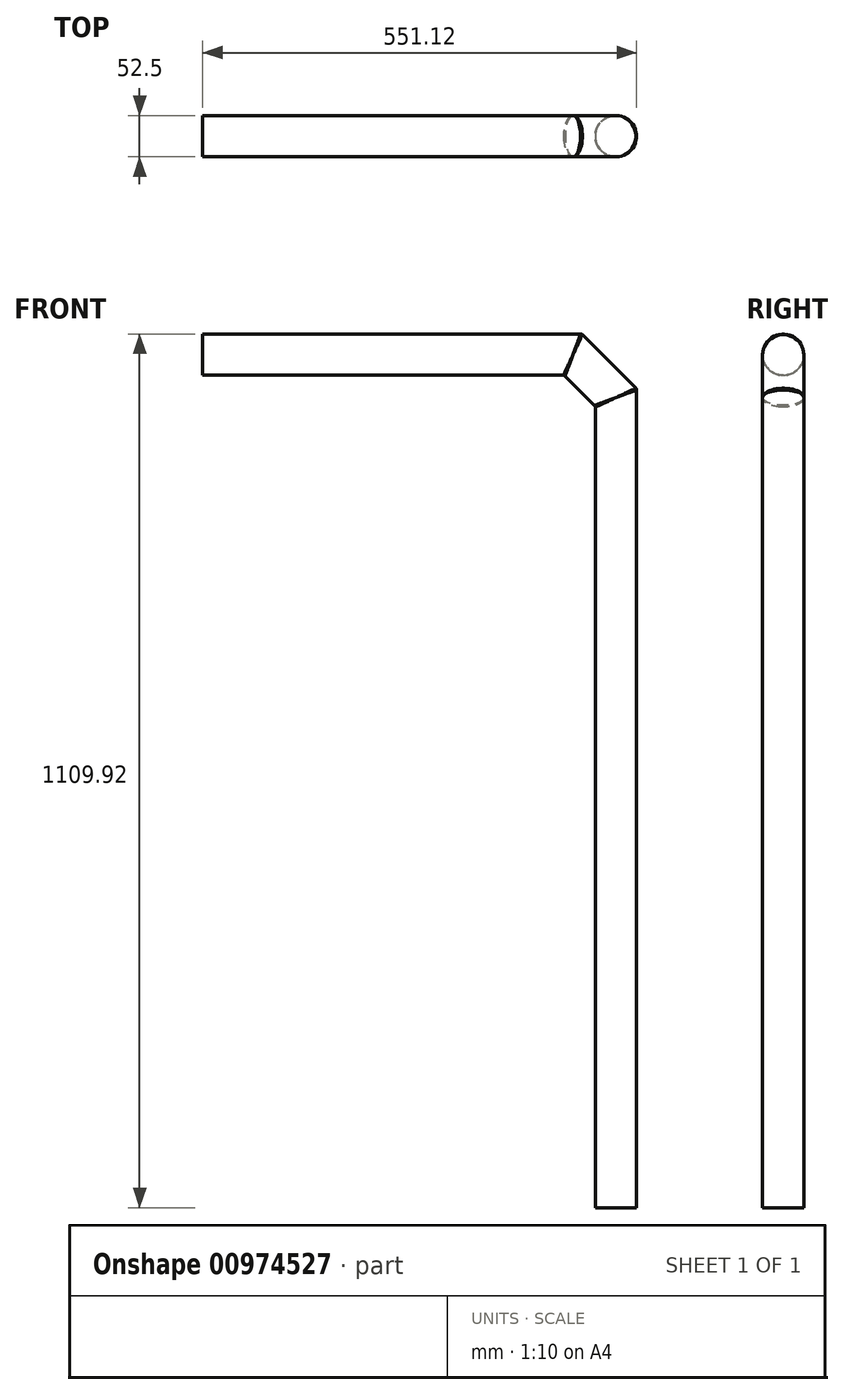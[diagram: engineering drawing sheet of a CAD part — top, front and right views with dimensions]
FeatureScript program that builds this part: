
annotation { "Feature Type Name" : "Feature", "Feature Type Description" : "" }
export const myFeature = defineFeature(function(context is Context, id is Id, definition is map)
    precondition{}
    {
        {
            var Q0;
            Q0=qCreatedBy(makeId("Right.planeOp"),FACE);
            var sketch = newSketch(context, id + "F0", { "sketchPlane" : qUnion([Q0])});
            skCircle(sketch, "E0", {"center": v(0, 0) * mm, "radius": 26.25 * mm});
            skSolve(sketch);
        }
        {
            var Q0;
            Q0=qCreatedBy(makeId("Front.planeOp"),FACE);
            var sketch = newSketch(context, id + "F1", { "sketchPlane" : qUnion([Q0])});
            skLineSegment(sketch, "E1", {"start": v(0, 0) * mm, "end": v(13.15, 0) * mm});
            skLineSegment(sketch, "E2", {"start": v(13.15, 0) * mm, "end": v(22.45, -9.3) * mm});
            skSolve(sketch);
        }
        {
            var Q0;
            Q0=makeQuery(id+"F0.imprint","IMPRINT",FACE,{"disambiguationData":[TD([[makeQuery(id+"F0.imprint","IMPRINT",EDGE,{"derivedFrom":sQuery(id+"F0.wireOp",EDGE,"E0")}),1.0]])]});
            var Q1;
            Q1=qConstructionFilter(qBodyType(qCreatedBy(id+"F1",EDGE),BodyType.WIRE),ConstructionObject.NO);
            sweep(context, id + "F2", {"profiles" : qUnion([Q0]), "path" : qUnion([Q1])});
        }
        {
            var Q0;
            Q0=makeQuery(id+"F2.opSweep","CAP_FACE",FACE,{"disambiguationData":[OSD([sQuery(id+"F0.wireOp",EDGE,"E0"),sQuery(id+"F1.wireOp",VERTEX,"E2.end")])],"isStart":false});
            extrude(context, id + "F3", {"entities" : qUnion([Q0]), "operationType" : NewBodyOperationType.ADD, "depth" : 50.8 * mm, "offsetDistance" : 25.4 * mm});
        }
        {
            var Q0;
            Q0=qCreatedBy(makeId("Front.planeOp"),FACE);
            var sketch = newSketch(context, id + "F4", { "sketchPlane" : qUnion([Q0])});
            skLineSegment(sketch, "E3", {"start": v(58.37, -45.22) * mm, "end": v(67.67, -54.52) * mm});
            skLineSegment(sketch, "E4", {"start": v(67.67, -54.52) * mm, "end": v(67.67, -67.67) * mm});
            skLineSegment(sketch, "E5.0", {"start": v(76.93, -26.66) * mm, "end": v(39.81, -63.78) * mm, "construction": true});
            skSolve(sketch);
        }
        {
            var Q0;
            Q0=makeQuery(id+"F3.opExtrude","CAP_FACE",FACE,{"disambiguationData":[OSD([sQuery(id+"F0.wireOp",EDGE,"E0"),sQuery(id+"F1.wireOp",VERTEX,"E2.end")])],"isStart":false});
            var Q1;
            Q1=qConstructionFilter(qBodyType(qCreatedBy(id+"F4",EDGE),BodyType.WIRE),ConstructionObject.NO);
            sweep(context, id + "F5", {"operationType" : NewBodyOperationType.ADD, "profiles" : qUnion([Q0]), "path" : qUnion([Q1])});
        }
        {
            var Q0;
            Q0=makeQuery(id+"F2.opSweep","CAP_FACE",FACE,{"disambiguationData":[OSD([sQuery(id+"F0.wireOp",EDGE,"E0"),sQuery(id+"F1.wireOp",VERTEX,"E1.start")])],"isStart":true});
            extrude(context, id + "F6", {"entities" : qUnion([Q0]), "operationType" : NewBodyOperationType.ADD, "depth" : 457.2 * mm, "offsetDistance" : 25.4 * mm});
        }
        {
            var Q0;
            Q0=makeQuery(id+"F5.opSweep","CAP_FACE",FACE,{"disambiguationData":[OSD([sQuery(id+"F0.wireOp",EDGE,"E0"),sQuery(id+"F1.wireOp",VERTEX,"E2.end"),sQuery(id+"F4.wireOp",VERTEX,"E4.end")])],"isStart":false});
            extrude(context, id + "F7", {"entities" : qUnion([Q0]), "operationType" : NewBodyOperationType.ADD, "depth" : 1016 * mm, "offsetDistance" : 25.4 * mm});
        }
        {
            var Q0;
            {var subQ0=sQuery(id+"F1.wireOp",VERTEX,"E2.end");var subQ1=sQuery(id+"F0.wireOp",EDGE,"E0");Q0=makeQuery(id+"F5.boolean.opBoolean","MERGE",FACE,{"derivedFrom":[makeQuery(id+"F3.boolean.opBoolean","MERGE",FACE,{"derivedFrom":[makeQuery(id+"F2.opSweep","SWEPT_FACE",FACE,{"disambiguationData":[OSD([subQ1,sQuery(id+"F1.wireOp",EDGE,"E2")])]}),makeQuery(id+"F3.opExtrude","SWEPT_FACE",FACE,{"disambiguationData":[OSD([subQ1,subQ0])]})]}),makeQuery(id+"F5.opSweep","SWEPT_FACE",FACE,{"disambiguationData":[OSD([subQ1,subQ0,sQuery(id+"F4.wireOp",EDGE,"E3")])]})]});}
            fillet(context, id + "F8", {"entities" : qUnion([Q0]), "tangentPropagation" : true, "radius" : 3.17 * mm, "defaultsChanged" : true, "vertexSettings" : [], "allowEdgeOverflow" : false});
        }
    });
